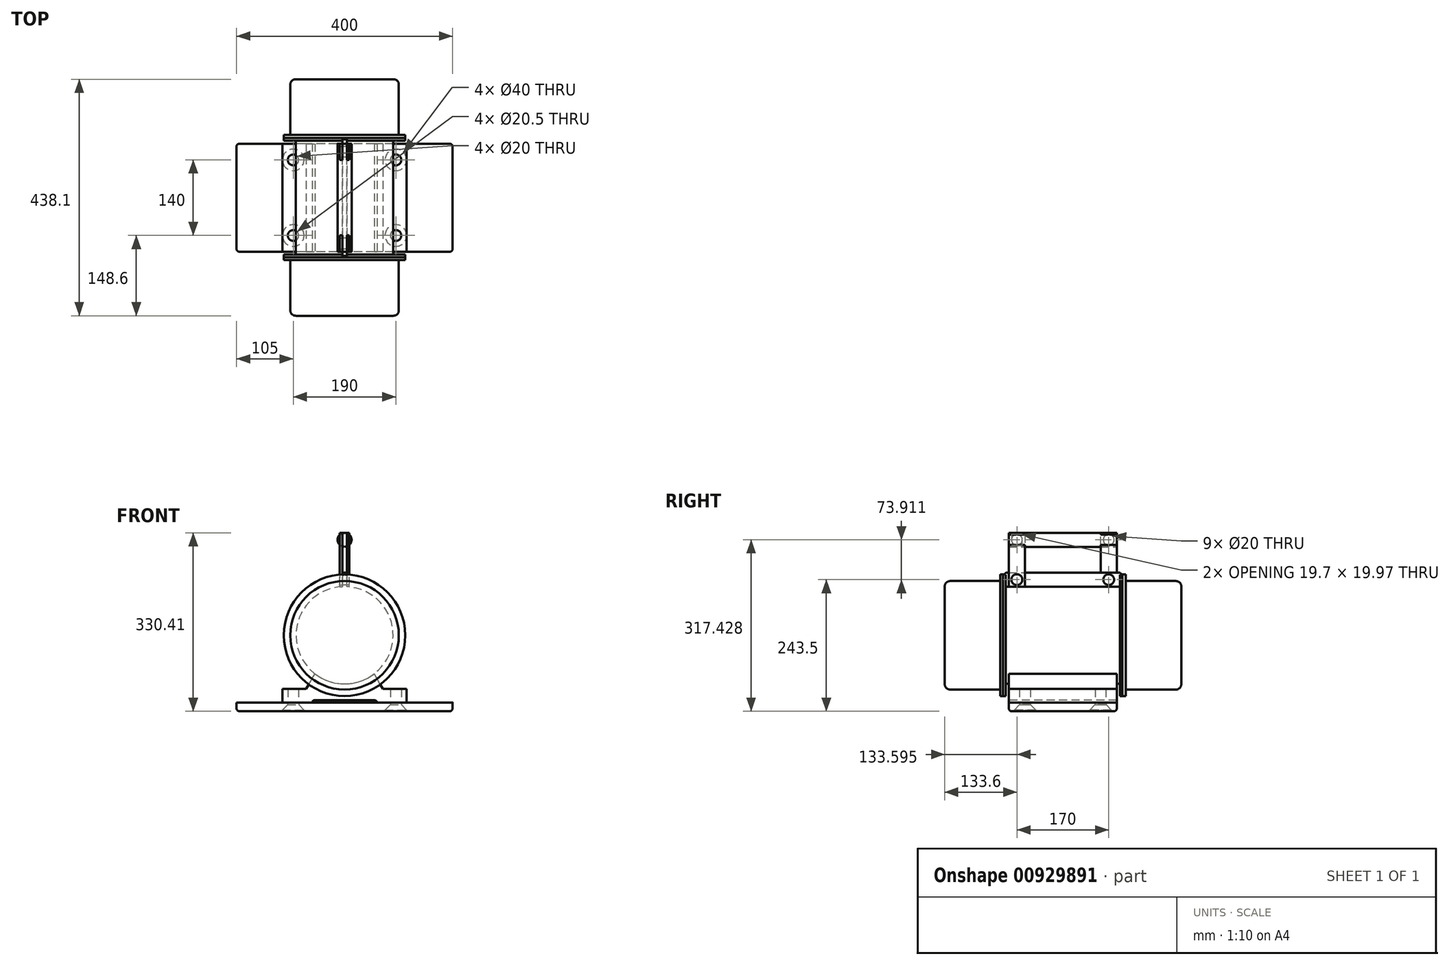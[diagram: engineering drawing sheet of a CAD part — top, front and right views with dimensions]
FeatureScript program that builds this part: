
annotation { "Feature Type Name" : "Feature", "Feature Type Description" : "" }
export const myFeature = defineFeature(function(context is Context, id is Id, definition is map)
    precondition{}
    {
        {
            var Q0;
            Q0=qCreatedBy(makeId("Front.planeOp"),FACE);
            var sketch = newSketch(context, id + "F0", { "sketchPlane" : qUnion([Q0])});
            skCircle(sketch, "E0", {"center": v(0, 0) * mm, "radius": 100.5 * mm});
            skSolve(sketch);
        }
        {
            var Q0;
            Q0=makeQuery(id+"F0.imprint","IMPRINT",FACE,{"disambiguationData":[TD([[makeQuery(id+"F0.imprint","IMPRINT",EDGE,{"derivedFrom":sQuery(id+"F0.wireOp",EDGE,"E0")}),1.0]])]});
            extrude(context, id + "F1", {"entities" : qUnion([Q0]), "depth" : 103 * mm, "offsetDistance" : 25 * mm});
        }
        {
            var Q0;
            Q0=makeQuery(id+"F1.opExtrude","CAP_EDGE",EDGE,{"disambiguationData":[OSD([sQuery(id+"F0.wireOp",EDGE,"E0")])],"isStart":false});
            fillet(context, id + "F2", {"entities" : qUnion([Q0]), "radius" : 10 * mm, "tangentPropagation" : true, "allowEdgeOverflow" : false});
        }
        {
            var Q0;
            Q0=makeQuery(id+"F1.opExtrude","CAP_FACE",FACE,{"disambiguationData":[OSD([sQuery(id+"F0.wireOp",EDGE,"E0")])],"isStart":true});
            var sketch = newSketch(context, id + "F3", { "sketchPlane" : qUnion([Q0])});
            skCircle(sketch, "E1", {"center": v(0, 0) * mm, "radius": 112.5 * mm});
            skSolve(sketch);
        }
        {
            var Q0;
            Q0=makeQuery(id+"F3.imprint","IMPRINT",FACE,{"disambiguationData":[TD([[makeQuery(id+"F3.imprint","IMPRINT",EDGE,{"derivedFrom":sQuery(id+"F3.wireOp",EDGE,"E1")}),1.0]])]});
            var Q1;
            Q1=makeQuery(id+"F3.imprint","IMPRINT",FACE,{"disambiguationData":[TD([[makeQuery(id+"F3.imprint","IMPRINT",EDGE,{"derivedFrom":makeQuery(id+"F1.opExtrude","CAP_EDGE",EDGE,{"disambiguationData":[OSD([sQuery(id+"F0.wireOp",EDGE,"E0")])],"isStart":true})}),-1.0]])]});
            extrude(context, id + "F4", {"entities" : qUnion([Q0, Q1]), "operationType" : NewBodyOperationType.ADD, "depth" : 5 * mm, "offsetDistance" : 25 * mm});
        }
        {
            var Q0;
            Q0=makeQuery(id+"F4.opExtrude","CAP_FACE",FACE,{"disambiguationData":[OSD([sQuery(id+"F3.wireOp",EDGE,"E1")])],"isStart":false});
            var sketch = newSketch(context, id + "F5", { "sketchPlane" : qUnion([Q0])});
            skCircle(sketch, "E2", {"center": v(0, 0) * mm, "radius": 112.5 * mm});
            skSolve(sketch);
        }
        {
            var Q0;
            Q0=makeQuery(id+"F5.imprint","IMPRINT",FACE,{"disambiguationData":[TD([[makeQuery(id+"F5.imprint","IMPRINT",EDGE,{"derivedFrom":sQuery(id+"F5.wireOp",EDGE,"E2")}),1.0]])]});
            extrude(context, id + "F6", {"entities" : qUnion([Q0]), "depth" : 5.1 * mm, "offsetDistance" : 25 * mm});
        }
        {
            var Q0;
            Q0=makeQuery(id+"F6.opExtrude","CAP_FACE",FACE,{"disambiguationData":[OSD([sQuery(id+"F5.wireOp",EDGE,"E2")])],"isStart":false});
            var sketch = newSketch(context, id + "F7", { "sketchPlane" : qUnion([Q0])});
            skCircle(sketch, "E3", {"center": v(0, 0) * mm, "radius": 90 * mm});
            skSolve(sketch);
        }
        {
            var Q0;
            Q0=makeQuery(id+"F7.imprint","IMPRINT",FACE,{"disambiguationData":[TD([[makeQuery(id+"F7.imprint","IMPRINT",EDGE,{"derivedFrom":sQuery(id+"F7.wireOp",EDGE,"E3")}),1.0]])]});
            extrude(context, id + "F8", {"entities" : qUnion([Q0]), "operationType" : NewBodyOperationType.ADD, "depth" : 211 * mm, "offsetDistance" : 25 * mm});
        }
        {
            var Q0;
            Q0=makeQuery(id+"F8.opExtrude","CAP_FACE",FACE,{"disambiguationData":[OSD([sQuery(id+"F7.wireOp",EDGE,"E3")])],"isStart":false});
            var sketch = newSketch(context, id + "F9", { "sketchPlane" : qUnion([Q0])});
            skCircle(sketch, "E4", {"center": v(0, 0) * mm, "radius": 112.5 * mm});
            skSolve(sketch);
        }
        {
            var Q0;
            Q0=makeQuery(id+"F9.imprint","IMPRINT",FACE,{"disambiguationData":[TD([[makeQuery(id+"F9.imprint","IMPRINT",EDGE,{"derivedFrom":makeQuery(id+"F8.opExtrude","CAP_EDGE",EDGE,{"disambiguationData":[OSD([sQuery(id+"F7.wireOp",EDGE,"E3")])],"isStart":false})}),1.0]])]});
            var Q1;
            Q1=makeQuery(id+"F9.imprint","IMPRINT",FACE,{"disambiguationData":[TD([[makeQuery(id+"F9.imprint","IMPRINT",EDGE,{"derivedFrom":sQuery(id+"F9.wireOp",EDGE,"E4")}),1.0]])]});
            extrude(context, id + "F10", {"entities" : qUnion([Q0, Q1]), "operationType" : NewBodyOperationType.ADD, "depth" : 5 * mm, "offsetDistance" : 25 * mm});
        }
        {
            var Q0;
            Q0=makeQuery(id+"F10.opExtrude","CAP_FACE",FACE,{"disambiguationData":[OSD([sQuery(id+"F9.wireOp",EDGE,"E4")])],"isStart":false});
            var sketch = newSketch(context, id + "F11", { "sketchPlane" : qUnion([Q0])});
            skCircle(sketch, "E5", {"center": v(0, 0) * mm, "radius": 112.5 * mm});
            skSolve(sketch);
        }
        {
            var Q0;
            Q0=makeQuery(id+"F11.imprint","IMPRINT",FACE,{"disambiguationData":[TD([[makeQuery(id+"F11.imprint","IMPRINT",EDGE,{"derivedFrom":sQuery(id+"F11.wireOp",EDGE,"E5")}),1.0]])]});
            extrude(context, id + "F12", {"entities" : qUnion([Q0]), "depth" : 6 * mm, "offsetDistance" : 25 * mm});
        }
        {
            var Q0;
            Q0=makeQuery(id+"F12.opExtrude","CAP_FACE",FACE,{"disambiguationData":[OSD([sQuery(id+"F11.wireOp",EDGE,"E5")])],"isStart":false});
            var sketch = newSketch(context, id + "F13", { "sketchPlane" : qUnion([Q0])});
            skCircle(sketch, "E6", {"center": v(0, 0) * mm, "radius": 100.5 * mm});
            skSolve(sketch);
        }
        {
            var Q0;
            Q0=makeQuery(id+"F13.imprint","IMPRINT",FACE,{"disambiguationData":[TD([[makeQuery(id+"F13.imprint","IMPRINT",EDGE,{"derivedFrom":sQuery(id+"F13.wireOp",EDGE,"E6")}),1.0]])]});
            extrude(context, id + "F14", {"entities" : qUnion([Q0]), "operationType" : NewBodyOperationType.ADD, "depth" : 103 * mm, "offsetDistance" : 25 * mm});
        }
        {
            var Q0;
            Q0=makeQuery(id+"F14.opExtrude","CAP_EDGE",EDGE,{"disambiguationData":[OSD([sQuery(id+"F13.wireOp",EDGE,"E6")])],"isStart":false});
            fillet(context, id + "F15", {"entities" : qUnion([Q0]), "radius" : 10 * mm, "tangentPropagation" : true, "allowEdgeOverflow" : false});
        }
        {
            var Q0;
            Q0=makeQuery(id+"F6.opExtrude","CAP_FACE",FACE,{"disambiguationData":[OSD([sQuery(id+"F5.wireOp",EDGE,"E2")])],"isStart":false});
            cPlane(context, id + "F16", {"entities" : qUnion([Q0]), "cplaneType" : CPlaneType.OFFSET, "offset" : (211 / 2) * mm, "width" : 150 * mm, "height" : 150 * mm});
        }
        {
            var Q0;
            Q0=qCreatedBy(id+"F16.planeOp",FACE);
            var sketch = newSketch(context, id + "F17", { "sketchPlane" : qUnion([Q0])});
            skLineSegment(sketch, "E7", {"start": v(0, 0) * mm, "end": v(151.06, 0) * mm, "construction": true});
            skLineSegment(sketch, "E8.0", {"start": v(-115, -124.5) * mm, "end": v(-60, -124.5) * mm});
            skLineSegment(sketch, "E9", {"start": v(0, 0) * mm, "end": v(0, -165.16) * mm, "construction": true});
            skLineSegment(sketch, "E10.0", {"start": v(-115, -99.5) * mm, "end": v(-115, -124.5) * mm});
            skLineSegment(sketch, "E11.0", {"start": v(115, -99.5) * mm, "end": v(115, -124.5) * mm});
            skCircle(sketch, "E12.0", {"center": v(0, 0) * mm, "radius": 90 * mm});
            skLineSegment(sketch, "E13.1", {"start": v(-56, -120.5) * mm, "end": v(56, -120.5) * mm});
            skLineSegment(sketch, "E14.trimOffspring", {"start": v(-60, -124.5) * mm, "end": v(-60, -124.5) * mm});
            skLineSegment(sketch, "E15.trimOffspring", {"start": v(60, -124.5) * mm, "end": v(60, -124.5) * mm});
            skLineSegment(sketch, "E16.trimOffspring", {"start": v(60, -124.5) * mm, "end": v(115, -124.5) * mm});
            skPoint(sketch, "E17.visualSharp", {"position": v(-60, -120.5) * mm});
            skArc(sketch, "E17.filletArc", {"start": v(-56, -120.5) * mm, "mid": v(-58.83, -121.67) * mm, "end": v(-60, -124.5) * mm});
            skPoint(sketch, "E18.visualSharp", {"position": v(60, -120.5) * mm});
            skArc(sketch, "E18.filletArc", {"start": v(60, -124.5) * mm, "mid": v(58.83, -121.67) * mm, "end": v(56, -120.5) * mm});
            skLineSegment(sketch, "E19", {"start": v(-115, -99.5) * mm, "end": v(-71.12, -99.5) * mm});
            skLineSegment(sketch, "E20.0", {"start": v(-71.12, -99.5) * mm, "end": v(-54.86, -71.34) * mm});
            skLineSegment(sketch, "E21.0", {"start": v(71.12, -99.5) * mm, "end": v(54.86, -71.34) * mm});
            skPoint(sketch, "E22.end.orphan", {"position": v(-80.63, -39.98) * mm});
            skLineSegment(sketch, "E23.trimOffspring", {"start": v(71.12, -99.5) * mm, "end": v(115, -99.5) * mm});
            skPoint(sketch, "E24.end.orphan", {"position": v(80.63, -39.98) * mm});
            skSolve(sketch);
        }
        {
            var Q0;
            Q0=makeQuery(id+"F17.imprint","IMPRINT",FACE,{"disambiguationData":[TD([[makeQuery(id+"F17.imprint","IMPRINT",EDGE,{"derivedFrom":sQuery(id+"F17.wireOp",EDGE,"E8.0")}),1.0]])]});
            extrude(context, id + "F18", {"entities" : qUnion([Q0]), "operationType" : NewBodyOperationType.ADD, "endBound" : BoundingType.SYMMETRIC, "depth" : 200 * mm, "offsetDistance" : 25 * mm});
        }
        {
            var Q0;
            Q0=makeQuery(id+"F18.opExtrude","SWEPT_FACE",FACE,{"disambiguationData":[OSD([sQuery(id+"F17.wireOp",EDGE,"E8.0")])]});
            var sketch = newSketch(context, id + "F19", { "sketchPlane" : qUnion([Q0])});
            skLineSegment(sketch, "E25.0", {"start": v(-115, -215.6) * mm, "end": v(-115, -15.6) * mm, "construction": true});
            skLineSegment(sketch, "E26.0", {"start": v(115, -215.6) * mm, "end": v(115, -15.6) * mm, "construction": true});
            skLineSegment(sketch, "E27", {"start": v(115, -15.6) * mm, "end": v(-115, -215.6) * mm, "construction": true});
            skLineSegment(sketch, "E28", {"start": v(115, -215.6) * mm, "end": v(-115, -15.6) * mm, "construction": true});
            skLineSegment(sketch, "E29.bottom", {"start": v(-95, -185.6) * mm, "end": v(95, -185.6) * mm, "construction": true});
            skLineSegment(sketch, "E29.top", {"start": v(-95, -45.6) * mm, "end": v(95, -45.6) * mm, "construction": true});
            skLineSegment(sketch, "E29.left", {"start": v(-95, -185.6) * mm, "end": v(-95, -45.6) * mm, "construction": true});
            skLineSegment(sketch, "E29.right", {"start": v(95, -185.6) * mm, "end": v(95, -45.6) * mm, "construction": true});
            skPoint(sketch, "E29.middle", {"position": v(0, -115.6) * mm});
            skCircle(sketch, "E30", {"center": v(95, -45.6) * mm, "radius": 10 * mm});
            skCircle(sketch, "E31", {"center": v(95, -185.6) * mm, "radius": 10 * mm});
            skCircle(sketch, "E32", {"center": v(-95, -185.6) * mm, "radius": 10 * mm});
            skCircle(sketch, "E33", {"center": v(-95, -45.6) * mm, "radius": 10 * mm});
            skSolve(sketch);
        }
        {
            var Q0;
            Q0=makeQuery(id+"F19.imprint","IMPRINT",FACE,{"disambiguationData":[TD([[makeQuery(id+"F19.imprint","IMPRINT",EDGE,{"derivedFrom":sQuery(id+"F19.wireOp",EDGE,"E30")}),1.0]])]});
            var Q1;
            Q1=makeQuery(id+"F19.imprint","IMPRINT",FACE,{"disambiguationData":[TD([[makeQuery(id+"F19.imprint","IMPRINT",EDGE,{"derivedFrom":sQuery(id+"F19.wireOp",EDGE,"E31")}),1.0]])]});
            var Q2;
            Q2=makeQuery(id+"F19.imprint","IMPRINT",FACE,{"disambiguationData":[TD([[makeQuery(id+"F19.imprint","IMPRINT",EDGE,{"derivedFrom":sQuery(id+"F19.wireOp",EDGE,"E33")}),1.0]])]});
            var Q3;
            Q3=makeQuery(id+"F19.imprint","IMPRINT",FACE,{"disambiguationData":[TD([[makeQuery(id+"F19.imprint","IMPRINT",EDGE,{"derivedFrom":sQuery(id+"F19.wireOp",EDGE,"E32")}),1.0]])]});
            extrude(context, id + "F20", {"entities" : qUnion([Q0, Q1, Q2, Q3]), "operationType" : NewBodyOperationType.REMOVE, "oppositeDirection" : true, "depth" : 25 * mm, "offsetDistance" : 25 * mm});
        }
        {
            var Q0;
            Q0=makeQuery(id+"F18.opExtrude","SWEPT_FACE",FACE,{"disambiguationData":[OSD([sQuery(id+"F17.wireOp",EDGE,"E16.trimOffspring")])]});
            var sketch = newSketch(context, id + "F21", { "sketchPlane" : qUnion([Q0])});
            skPoint(sketch, "E34.0", {"position": v(0, -115.6) * mm});
            skLineSegment(sketch, "E35.bottom", {"start": v(200, -15.6) * mm, "end": v(-200, -15.6) * mm});
            skLineSegment(sketch, "E35.top", {"start": v(200, -215.6) * mm, "end": v(-200, -215.6) * mm});
            skLineSegment(sketch, "E35.left", {"start": v(200, -15.6) * mm, "end": v(200, -215.6) * mm});
            skLineSegment(sketch, "E35.right", {"start": v(-200, -15.6) * mm, "end": v(-200, -215.6) * mm});
            skCircle(sketch, "E36.0", {"center": v(-95, -185.6) * mm, "radius": 10 * mm});
            skCircle(sketch, "E37.0", {"center": v(-95, -45.6) * mm, "radius": 10 * mm});
            skCircle(sketch, "E38.0", {"center": v(95, -185.6) * mm, "radius": 10 * mm});
            skCircle(sketch, "E39.0", {"center": v(95, -45.6) * mm, "radius": 10 * mm});
            skSolve(sketch);
        }
        {
            var Q0;
            Q0 = qSketchRegion(id + "F21", true);
            var Q1;
            Q1=makeQuery(id+"F21.imprint","IMPRINT",FACE,{"disambiguationData":[TD([[makeQuery(id+"F21.imprint","IMPRINT",EDGE,{"derivedFrom":sQuery(id+"F21.wireOp",EDGE,"E37.0")}),1.0]])]});
            var Q2;
            Q2=makeQuery(id+"F21.imprint","IMPRINT",FACE,{"disambiguationData":[TD([[makeQuery(id+"F21.imprint","IMPRINT",EDGE,{"derivedFrom":sQuery(id+"F21.wireOp",EDGE,"E39.0")}),1.0]])]});
            var Q3;
            Q3=makeQuery(id+"F21.imprint","IMPRINT",FACE,{"disambiguationData":[TD([[makeQuery(id+"F21.imprint","IMPRINT",EDGE,{"derivedFrom":sQuery(id+"F21.wireOp",EDGE,"E38.0")}),1.0]])]});
            var Q4;
            Q4=makeQuery(id+"F21.imprint","IMPRINT",FACE,{"disambiguationData":[TD([[makeQuery(id+"F21.imprint","IMPRINT",EDGE,{"derivedFrom":sQuery(id+"F21.wireOp",EDGE,"E36.0")}),1.0]])]});
            extrude(context, id + "F22", {"entities" : qUnion([Q0, Q1, Q2, Q3, Q4]), "depth" : 16 * mm, "offsetDistance" : 25 * mm});
        }
        {
            var Q0;
            Q0=makeQuery(id+"F22.opExtrude","CAP_EDGE",EDGE,{"disambiguationData":[OSD([sQuery(id+"F21.wireOp",EDGE,"E35.top")])],"isStart":false});
            var Q1;
            Q1=makeQuery(id+"F22.opExtrude","CAP_EDGE",EDGE,{"disambiguationData":[OSD([sQuery(id+"F21.wireOp",EDGE,"E35.right")])],"isStart":false});
            var Q2;
            Q2=makeQuery(id+"F22.opExtrude","CAP_EDGE",EDGE,{"disambiguationData":[OSD([sQuery(id+"F21.wireOp",EDGE,"E35.bottom")])],"isStart":false});
            var Q3;
            Q3=makeQuery(id+"F22.opExtrude","CAP_EDGE",EDGE,{"disambiguationData":[OSD([sQuery(id+"F21.wireOp",EDGE,"E35.left")])],"isStart":false});
            var Q4;
            Q4=makeQuery(id+"F22.opExtrude","SWEPT_EDGE",EDGE,{"disambiguationData":[OSD([sQuery(id+"F21.wireOp",EDGE,"E35.top"),sQuery(id+"F21.wireOp",EDGE,"E35.right")])]});
            var Q5;
            Q5=makeQuery(id+"F22.opExtrude","SWEPT_EDGE",EDGE,{"disambiguationData":[OSD([sQuery(id+"F21.wireOp",EDGE,"E35.bottom"),sQuery(id+"F21.wireOp",EDGE,"E35.right")])]});
            var Q6;
            Q6=makeQuery(id+"F22.opExtrude","SWEPT_EDGE",EDGE,{"disambiguationData":[OSD([sQuery(id+"F21.wireOp",EDGE,"E35.top"),sQuery(id+"F21.wireOp",EDGE,"E35.left")])]});
            var Q7;
            Q7=makeQuery(id+"F22.opExtrude","SWEPT_EDGE",EDGE,{"disambiguationData":[OSD([sQuery(id+"F21.wireOp",EDGE,"E35.bottom"),sQuery(id+"F21.wireOp",EDGE,"E35.left")])]});
            fillet(context, id + "F23", {"entities" : qUnion([Q0, Q1, Q2, Q3, Q4, Q5, Q6, Q7]), "radius" : 5 * mm, "tangentPropagation" : true, "allowEdgeOverflow" : false});
        }
        {
            var Q0;
            Q0=makeQuery(id+"F22.opExtrude","CAP_FACE",FACE,{"disambiguationData":[OSD([sQuery(id+"F21.wireOp",EDGE,"E35.bottom"),sQuery(id+"F21.wireOp",EDGE,"E35.top"),sQuery(id+"F21.wireOp",EDGE,"E35.left"),sQuery(id+"F21.wireOp",EDGE,"E35.right")])],"isStart":false});
            var sketch = newSketch(context, id + "F24", { "sketchPlane" : qUnion([Q0])});
            skPoint(sketch, "E40.0", {"position": v(-95, -45.6) * mm});
            skPoint(sketch, "E41.0", {"position": v(95, -45.6) * mm});
            skPoint(sketch, "E42.0", {"position": v(-95, -185.6) * mm});
            skPoint(sketch, "E43.0", {"position": v(95, -185.6) * mm});
            skCircle(sketch, "E44", {"center": v(-95, -45.6) * mm, "radius": 20 * mm});
            skCircle(sketch, "E45", {"center": v(95, -45.6) * mm, "radius": 20 * mm});
            skCircle(sketch, "E46", {"center": v(95, -185.6) * mm, "radius": 20 * mm});
            skCircle(sketch, "E47", {"center": v(-95, -185.6) * mm, "radius": 20 * mm});
            skSolve(sketch);
        }
        {
            var Q0;
            Q0=makeQuery(id+"F22.opExtrude","CAP_FACE",FACE,{"disambiguationData":[OSD([sQuery(id+"F21.wireOp",EDGE,"E35.bottom"),sQuery(id+"F21.wireOp",EDGE,"E35.top"),sQuery(id+"F21.wireOp",EDGE,"E35.left"),sQuery(id+"F21.wireOp",EDGE,"E35.right")])],"isStart":false});
            cPlane(context, id + "F25", {"entities" : qUnion([Q0]), "cplaneType" : CPlaneType.OFFSET, "offset" : 2 * mm, "oppositeDirection" : true, "width" : 150 * mm, "height" : 150 * mm});
        }
        {
            var Q0;
            Q0=qCreatedBy(id+"F25.planeOp",FACE);
            var sketch = newSketch(context, id + "F26", { "sketchPlane" : qUnion([Q0])});
            skPoint(sketch, "E48.0", {"position": v(95, -185.6) * mm});
            skPoint(sketch, "E49.0", {"position": v(-95, -185.6) * mm});
            skPoint(sketch, "E50.0", {"position": v(95, -45.6) * mm});
            skPoint(sketch, "E51.0", {"position": v(-95, -45.6) * mm});
            skSolve(sketch);
        }
        {
            var Q0;
            Q0=makeQuery(id+"F24.imprint","IMPRINT",FACE,{"disambiguationData":[TD([[makeQuery(id+"F24.imprint","IMPRINT",EDGE,{"derivedFrom":sQuery(id+"F24.wireOp",EDGE,"E44")}),1.0]])]});
            var Q1;
            Q1=makeQuery(id+"F24.imprint","IMPRINT",FACE,{"disambiguationData":[TD([[makeQuery(id+"F24.imprint","IMPRINT",EDGE,{"derivedFrom":sQuery(id+"F24.wireOp",EDGE,"E45")}),1.0]])]});
            var Q2;
            Q2=makeQuery(id+"F24.imprint","IMPRINT",FACE,{"disambiguationData":[TD([[makeQuery(id+"F24.imprint","IMPRINT",EDGE,{"derivedFrom":sQuery(id+"F24.wireOp",EDGE,"E47")}),1.0]])]});
            var Q3;
            Q3=makeQuery(id+"F24.imprint","IMPRINT",FACE,{"disambiguationData":[TD([[makeQuery(id+"F24.imprint","IMPRINT",EDGE,{"derivedFrom":sQuery(id+"F24.wireOp",EDGE,"E46")}),1.0]])]});
            extrude(context, id + "F27", {"entities" : qUnion([Q0, Q1, Q2, Q3]), "operationType" : NewBodyOperationType.REMOVE, "oppositeDirection" : true, "depth" : 2 * mm, "offsetDistance" : 25 * mm});
        }
        {
            var Q0;
            Q0=sQuery(id+"F26.wireOp",VERTEX,"E51.0");
            var Q1;
            Q1=sQuery(id+"F26.wireOp",VERTEX,"E50.0");
            var Q2;
            Q2=sQuery(id+"F26.wireOp",VERTEX,"E49.0");
            var Q3;
            Q3=sQuery(id+"F26.wireOp",VERTEX,"E48.0");
            var Q4;
            Q4=makeQuery(id+"F22.opExtrude","SWEPT_BODY",BODY,{"disambiguationData":[OSD([sQuery(id+"F21.wireOp",EDGE,"E35.bottom"),sQuery(id+"F21.wireOp",EDGE,"E35.top"),sQuery(id+"F21.wireOp",EDGE,"E35.left"),sQuery(id+"F21.wireOp",EDGE,"E35.right")])]});
            hole(context, id + "F28", {"style" : HoleStyle.C_SINK, "endStyle" : HoleEndStyle.BLIND, "standardTappedOrClearance" : lookupTablePath({ "standard" : "ISO", "size" : "20.5", "type" : "Drilled" }), "standardBlindInLast" : lookupTablePath({ "standard" : "ISO", "size" : "20.5", "type" : "Drilled" }), "holeDiameter" : 20.5 * mm, "cSinkDiameter" : 40 * mm, "cSinkAngle" : 90 * degree, "majorDiameter" : 5 * mm, "holeDepth" : 25 * mm, "isTappedThrough" : true, "tappedDepth" : 21.25 * mm, "tapClearance" : 3, "startFromSketch" : true, "locations" : qUnion([Q0, Q1, Q2, Q3]), "scope" : qUnion([Q4])});
        }
        {
            var Q0;
            Q0=qCreatedBy(makeId("Right.planeOp"),FACE);
            var sketch = newSketch(context, id + "F29", { "sketchPlane" : qUnion([Q0])});
            skLineSegment(sketch, "E52.bottom", {"start": v(11.9, 116) * mm, "end": v(219.8, 116) * mm});
            skLineSegment(sketch, "E53", {"start": v(115.6, 116) * mm, "end": v(115.6, 90) * mm, "construction": true});
            skPoint(sketch, "E54.orphan", {"position": v(30.6, 112.5) * mm});
            skPoint(sketch, "E55.orphan", {"position": v(200.6, 112.5) * mm});
            skCircle(sketch, "E56", {"center": v(30.6, 103) * mm, "radius": 10 * mm});
            skCircle(sketch, "E57", {"center": v(200.6, 103) * mm, "radius": 10 * mm});
            skLineSegment(sketch, "E58.0", {"start": v(7.9, 82) * mm, "end": v(223.8, 82) * mm});
            skLineSegment(sketch, "E59", {"start": v(7.9, 82) * mm, "end": v(7.9, 112) * mm});
            skLineSegment(sketch, "E60", {"start": v(223.8, 82) * mm, "end": v(223.8, 112) * mm});
            skPoint(sketch, "E61.visualSharp", {"position": v(7.9, 116) * mm});
            skArc(sketch, "E61.filletArc", {"start": v(11.9, 116) * mm, "mid": v(9.06, 114.83) * mm, "end": v(7.9, 112) * mm});
            skPoint(sketch, "E62.visualSharp", {"position": v(223.8, 116) * mm});
            skArc(sketch, "E62.filletArc", {"start": v(223.8, 112) * mm, "mid": v(222.64, 114.83) * mm, "end": v(219.8, 116) * mm});
            skSolve(sketch);
        }
        {
            var Q0;
            Q0=makeQuery(id+"F29.imprint","IMPRINT",FACE,{"disambiguationData":[TD([[makeQuery(id+"F29.imprint","IMPRINT",EDGE,{"derivedFrom":sQuery(id+"F29.wireOp",EDGE,"E52.bottom")}),-1.0]])]});
            extrude(context, id + "F30", {"entities" : qUnion([Q0]), "operationType" : NewBodyOperationType.ADD, "endBound" : BoundingType.SYMMETRIC, "depth" : 8 * mm, "offsetDistance" : 25 * mm});
        }
        {
            var Q0;
            Q0=makeQuery(id+"F30.opExtrude","CAP_FACE",FACE,{"disambiguationData":[OSD([sQuery(id+"F29.wireOp",EDGE,"E52.bottom"),sQuery(id+"F29.wireOp",EDGE,"E56"),sQuery(id+"F29.wireOp",EDGE,"E57"),sQuery(id+"F29.wireOp",EDGE,"E58.0"),sQuery(id+"F29.wireOp",EDGE,"E59"),sQuery(id+"F29.wireOp",EDGE,"E60"),sQuery(id+"F29.wireOp",EDGE,"E61.filletArc"),sQuery(id+"F29.wireOp",EDGE,"E62.filletArc")])],"isStart":false});
            var sketch = newSketch(context, id + "F31", { "sketchPlane" : qUnion([Q0])});
            skLineSegment(sketch, "E63.bottom", {"start": v(45.6, 89.91) * mm, "end": v(15.6, 89.91) * mm});
            skLineSegment(sketch, "E63.top", {"start": v(45.6, 189.91) * mm, "end": v(15.6, 189.91) * mm});
            skLineSegment(sketch, "E63.left", {"start": v(45.6, 89.91) * mm, "end": v(45.6, 189.91) * mm});
            skLineSegment(sketch, "E63.right", {"start": v(15.6, 89.91) * mm, "end": v(15.6, 189.91) * mm});
            skCircle(sketch, "E64.0", {"center": v(30.6, 103) * mm, "radius": 10 * mm});
            skCircle(sketch, "E65.0", {"center": v(200.6, 103) * mm, "radius": 10 * mm});
            skLineSegment(sketch, "E66.MirrorCS", {"start": v(185.6, 189.91) * mm, "end": v(215.6, 189.91) * mm});
            skLineSegment(sketch, "E67.MirrorCS", {"start": v(185.6, 89.91) * mm, "end": v(215.6, 89.91) * mm});
            skLineSegment(sketch, "E68.MirrorCS", {"start": v(185.6, 89.91) * mm, "end": v(185.6, 189.91) * mm});
            skLineSegment(sketch, "E69.MirrorCS", {"start": v(215.6, 89.91) * mm, "end": v(215.6, 189.91) * mm});
            skCircle(sketch, "E70", {"center": v(30.6, 176.91) * mm, "radius": 10 * mm});
            skPoint(sketch, "E70.centerSnap0", {"position": v(30.6, 189.91) * mm});
            skCircle(sketch, "E71.MirrorC", {"center": v(200.6, 176.91) * mm, "radius": 10 * mm});
            skSolve(sketch);
        }
        {
            var Q0;
            {var subQ0=sQuery(id+"F31.wireOp",EDGE,"E63.top");Q0=makeQuery(id+"F31.imprint","IMPRINT",FACE,{"disambiguationData":[TD([[makeQuery(id+"F31.imprint","IMPRINT",EDGE,{"derivedFrom":subQ0}),1.0]])]});}
            var Q1;
            {var subQ1=sQuery(id+"F31.wireOp",EDGE,"E63.bottom");Q1=makeQuery(id+"F31.imprint","IMPRINT",FACE,{"disambiguationData":[TD([[makeQuery(id+"F31.imprint","IMPRINT",EDGE,{"derivedFrom":subQ1}),-1.0]])]});}
            var Q2;
            {var subQ0=sQuery(id+"F31.wireOp",EDGE,"E66.MirrorCS");Q2=makeQuery(id+"F31.imprint","IMPRINT",FACE,{"disambiguationData":[TD([[makeQuery(id+"F31.imprint","IMPRINT",EDGE,{"derivedFrom":subQ0}),-1.0]])]});}
            var Q3;
            Q3=makeQuery(id+"F31.imprint","IMPRINT",FACE,{"disambiguationData":[TD([[makeQuery(id+"F31.imprint","IMPRINT",EDGE,{"derivedFrom":sQuery(id+"F31.wireOp",EDGE,"E65.0")}),-1.0]])]});
            extrude(context, id + "F32", {"entities" : qUnion([Q0, Q1, Q2, Q3]), "depth" : 5 * mm, "offsetDistance" : 25 * mm});
        }
        {
            var Q0;
            Q0=makeQuery(id+"F30.opExtrude","CAP_FACE",FACE,{"disambiguationData":[OSD([sQuery(id+"F29.wireOp",EDGE,"E52.bottom"),sQuery(id+"F29.wireOp",EDGE,"E56"),sQuery(id+"F29.wireOp",EDGE,"E57"),sQuery(id+"F29.wireOp",EDGE,"E58.0"),sQuery(id+"F29.wireOp",EDGE,"E59"),sQuery(id+"F29.wireOp",EDGE,"E60"),sQuery(id+"F29.wireOp",EDGE,"E61.filletArc"),sQuery(id+"F29.wireOp",EDGE,"E62.filletArc")])],"isStart":true});
            var sketch = newSketch(context, id + "F33", { "sketchPlane" : qUnion([Q0])});
            skLineSegment(sketch, "E72.0.0", {"start": v(-185.6, 89.91) * mm, "end": v(-185.6, 189.91) * mm});
            skLineSegment(sketch, "E72.0.1", {"start": v(-185.6, 189.91) * mm, "end": v(-215.6, 189.91) * mm});
            skLineSegment(sketch, "E72.0.2", {"start": v(-215.6, 189.91) * mm, "end": v(-215.6, 89.91) * mm});
            skLineSegment(sketch, "E72.0.3", {"start": v(-215.6, 89.91) * mm, "end": v(-185.6, 89.91) * mm});
            skLineSegment(sketch, "E73.0.0", {"start": v(-15.6, 89.91) * mm, "end": v(-15.6, 189.91) * mm});
            skLineSegment(sketch, "E73.0.1", {"start": v(-15.6, 189.91) * mm, "end": v(-45.6, 189.91) * mm});
            skLineSegment(sketch, "E73.0.2", {"start": v(-45.6, 189.91) * mm, "end": v(-45.6, 89.91) * mm});
            skLineSegment(sketch, "E73.0.3", {"start": v(-45.6, 89.91) * mm, "end": v(-15.6, 89.91) * mm});
            skCircle(sketch, "E74.0", {"center": v(-30.6, 103) * mm, "radius": 10 * mm});
            skCircle(sketch, "E75.0", {"center": v(-200.6, 103) * mm, "radius": 10 * mm});
            skCircle(sketch, "E76.0", {"center": v(-200.6, 176.91) * mm, "radius": 10 * mm});
            skCircle(sketch, "E77.0", {"center": v(-30.6, 176.91) * mm, "radius": 10 * mm});
            skSolve(sketch);
        }
        {
            var Q0;
            {var subQ0=sQuery(id+"F33.wireOp",EDGE,"E72.0.1");Q0=makeQuery(id+"F33.imprint","IMPRINT",FACE,{"disambiguationData":[TD([[makeQuery(id+"F33.imprint","IMPRINT",EDGE,{"derivedFrom":subQ0}),1.0]])]});}
            var Q1;
            {var subQ0=sQuery(id+"F33.wireOp",EDGE,"E72.0.3");Q1=makeQuery(id+"F33.imprint","IMPRINT",FACE,{"disambiguationData":[TD([[makeQuery(id+"F33.imprint","IMPRINT",EDGE,{"derivedFrom":subQ0}),1.0]])]});}
            var Q2;
            {var subQ0=sQuery(id+"F33.wireOp",EDGE,"E73.0.1");Q2=makeQuery(id+"F33.imprint","IMPRINT",FACE,{"disambiguationData":[TD([[makeQuery(id+"F33.imprint","IMPRINT",EDGE,{"derivedFrom":subQ0}),1.0]])]});}
            var Q3;
            {var subQ0=sQuery(id+"F33.wireOp",EDGE,"E73.0.3");Q3=makeQuery(id+"F33.imprint","IMPRINT",FACE,{"disambiguationData":[TD([[makeQuery(id+"F33.imprint","IMPRINT",EDGE,{"derivedFrom":subQ0}),1.0]])]});}
            extrude(context, id + "F34", {"entities" : qUnion([Q0, Q1, Q2, Q3]), "depth" : 5 * mm, "offsetDistance" : 25 * mm});
        }
        {
            var Q0;
            Q0=qCreatedBy(makeId("Right.planeOp"),FACE);
            var sketch = newSketch(context, id + "F35", { "sketchPlane" : qUnion([Q0])});
            skPoint(sketch, "E78.0", {"position": v(215.6, 189.91) * mm});
            skPoint(sketch, "E79.0", {"position": v(15.6, 189.91) * mm});
            skLineSegment(sketch, "E80.bottom", {"start": v(215.6, 189.91) * mm, "end": v(15.6, 189.91) * mm});
            skLineSegment(sketch, "E80.left", {"start": v(215.6, 189.91) * mm, "end": v(215.6, 176.91) * mm});
            skLineSegment(sketch, "E80.right", {"start": v(15.6, 189.91) * mm, "end": v(15.6, 176.91) * mm});
            skCircle(sketch, "E81.0", {"center": v(200.6, 176.91) * mm, "radius": 10 * mm, "construction": true});
            skCircle(sketch, "E82.0", {"center": v(30.6, 176.91) * mm, "radius": 10 * mm, "construction": true});
            skLineSegment(sketch, "E83", {"start": v(215.6, 176.91) * mm, "end": v(15.6, 176.91) * mm});
            skPoint(sketch, "E84.orphan", {"position": v(215.6, 163.91) * mm});
            skPoint(sketch, "E85.orphan", {"position": v(15.6, 163.91) * mm});
            skSolve(sketch);
        }
        {
            var Q0;
            Q0=makeQuery(id+"F35.imprint","IMPRINT",FACE,{"disambiguationData":[TD([[makeQuery(id+"F35.imprint","IMPRINT",EDGE,{"derivedFrom":sQuery(id+"F35.wireOp",EDGE,"E80.bottom")}),1.0]])]});
            var Q1;
            Q1=sQuery(id+"F35.wireOp",EDGE,"E83");
            revolve(context, id + "F36", {"surfaceOperationType" : NewSurfaceOperationType.NEW, "entities" : qUnion([Q0]), "axis" : qUnion([Q1]), "revolveType" : RevolveType.FULL});
        }
        {
            var Q0;
            Q0=makeQuery(id+"F34.opExtrude","SWEPT_BODY",BODY,{"disambiguationData":[OSD([sQuery(id+"F33.wireOp",EDGE,"E73.0.0"),sQuery(id+"F33.wireOp",EDGE,"E73.0.1"),sQuery(id+"F33.wireOp",EDGE,"E73.0.2"),sQuery(id+"F33.wireOp",EDGE,"E73.0.3"),sQuery(id+"F33.wireOp",EDGE,"E74.0"),sQuery(id+"F33.wireOp",EDGE,"E77.0")])]});
            var Q1;
            Q1=makeQuery(id+"F32.opExtrude","SWEPT_BODY",BODY,{"disambiguationData":[OSD([sQuery(id+"F31.wireOp",EDGE,"E63.bottom"),sQuery(id+"F31.wireOp",EDGE,"E63.top"),sQuery(id+"F31.wireOp",EDGE,"E63.left"),sQuery(id+"F31.wireOp",EDGE,"E63.right"),sQuery(id+"F31.wireOp",EDGE,"E64.0"),sQuery(id+"F31.wireOp",EDGE,"E70")])]});
            var Q2;
            Q2=makeQuery(id+"F34.opExtrude","SWEPT_BODY",BODY,{"disambiguationData":[OSD([sQuery(id+"F33.wireOp",EDGE,"E72.0.0"),sQuery(id+"F33.wireOp",EDGE,"E72.0.1"),sQuery(id+"F33.wireOp",EDGE,"E72.0.2"),sQuery(id+"F33.wireOp",EDGE,"E72.0.3"),sQuery(id+"F33.wireOp",EDGE,"E75.0"),sQuery(id+"F33.wireOp",EDGE,"E76.0")])]});
            var Q3;
            Q3=makeQuery(id+"F32.opExtrude","SWEPT_BODY",BODY,{"disambiguationData":[OSD([sQuery(id+"F31.wireOp",EDGE,"E66.MirrorCS"),sQuery(id+"F31.wireOp",EDGE,"E65.0"),sQuery(id+"F31.wireOp",EDGE,"E67.MirrorCS"),sQuery(id+"F31.wireOp",EDGE,"E68.MirrorCS"),sQuery(id+"F31.wireOp",EDGE,"E69.MirrorCS"),sQuery(id+"F31.wireOp",EDGE,"E71.MirrorC")])]});
            var Q4;
            Q4=makeQuery(id+"F36.opRevolve","SWEPT_BODY",BODY,{"disambiguationData":[OSD([sQuery(id+"F35.wireOp",EDGE,"E80.bottom"),sQuery(id+"F35.wireOp",EDGE,"E80.left"),sQuery(id+"F35.wireOp",EDGE,"E80.right"),sQuery(id+"F35.wireOp",EDGE,"E83")])]});
            booleanBodies(context, id + "F37", {"operationType" : BooleanOperationType.SUBTRACTION, "tools" : qUnion([Q0, Q1, Q2, Q3]), "targets" : qUnion([Q4]), "keepTools" : true});
        }
    });
